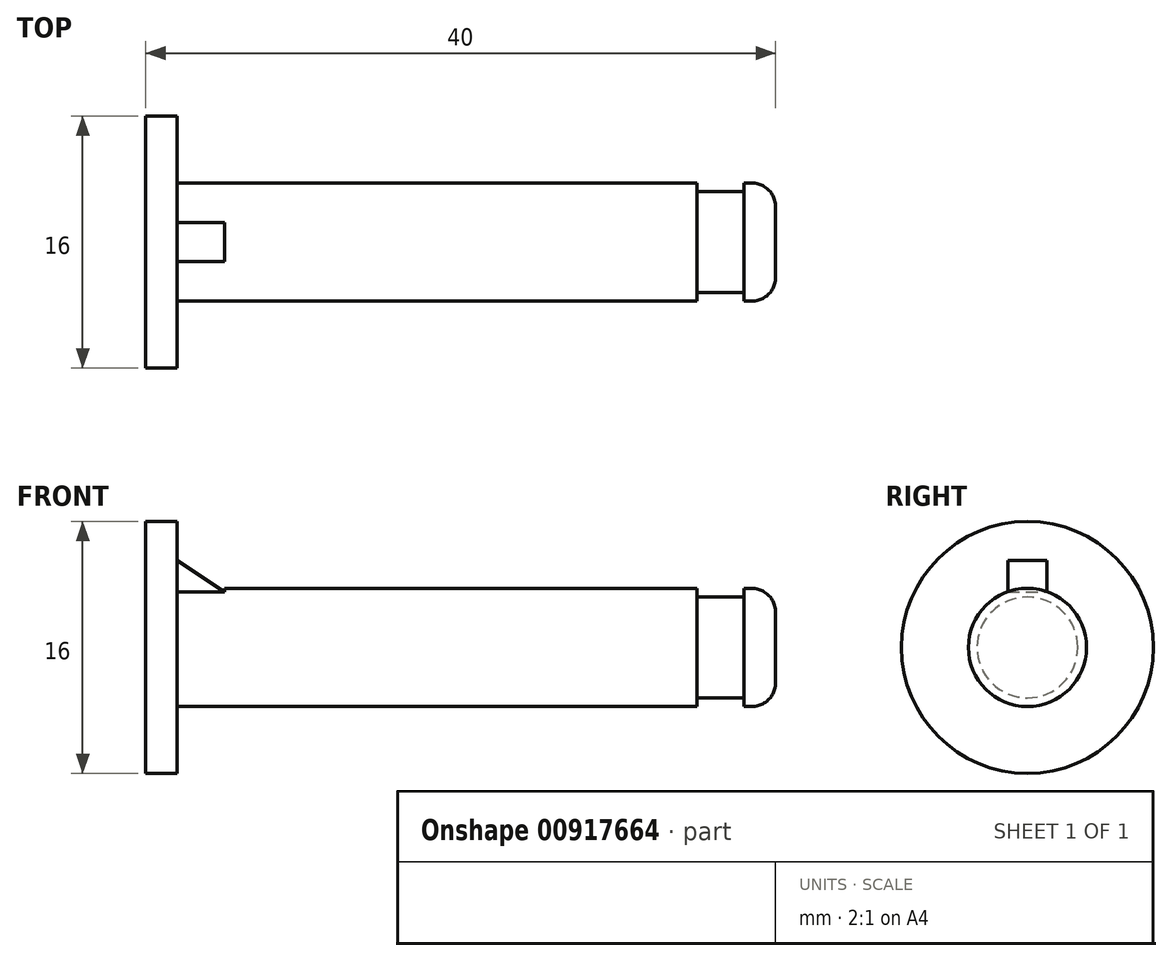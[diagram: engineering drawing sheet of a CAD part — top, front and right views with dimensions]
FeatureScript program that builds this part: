
annotation { "Feature Type Name" : "Feature", "Feature Type Description" : "" }
export const myFeature = defineFeature(function(context is Context, id is Id, definition is map)
    precondition{}
    {
        {
            var Q0;
            Q0=qCreatedBy(makeId("Front.planeOp"),FACE);
            var sketch = newSketch(context, id + "F0", { "sketchPlane" : qUnion([Q0])});
            skLineSegment(sketch, "E0", {"start": v(0, 0) * mm, "end": v(0, 8) * mm});
            skLineSegment(sketch, "E1", {"start": v(0, 8) * mm, "end": v(2, 8) * mm});
            skLineSegment(sketch, "E2", {"start": v(2, 8) * mm, "end": v(2, 3.75) * mm});
            skLineSegment(sketch, "E3", {"start": v(2, 3.75) * mm, "end": v(35, 3.75) * mm});
            skLineSegment(sketch, "E4", {"start": v(35, 3.75) * mm, "end": v(35, 3.2) * mm});
            skLineSegment(sketch, "E5", {"start": v(35, 3.2) * mm, "end": v(38, 3.2) * mm});
            skLineSegment(sketch, "E6", {"start": v(38, 3.2) * mm, "end": v(38, 3.75) * mm});
            skLineSegment(sketch, "E7", {"start": v(38, 3.75) * mm, "end": v(40, 3.75) * mm});
            skLineSegment(sketch, "E8", {"start": v(40, 3.75) * mm, "end": v(40, 0) * mm});
            skLineSegment(sketch, "E9", {"start": v(0, 0) * mm, "end": v(40, 0) * mm});
            skSolve(sketch);
        }
        {
            var Q0;
            Q0 = qSketchRegion(id + "F0", true);
            var Q1;
            Q1=sQuery(id+"F0.wireOp",EDGE,"E9");
            revolve(context, id + "F1", {"surfaceOperationType" : NewSurfaceOperationType.NEW, "entities" : qUnion([Q0]), "axis" : qUnion([Q1]), "revolveType" : RevolveType.FULL});
        }
        {
            var Q0;
            Q0=makeQuery(id+"F1.opRevolve","SWEPT_EDGE",EDGE,{"disambiguationData":[OSD([sQuery(id+"F0.wireOp",EDGE,"E7"),sQuery(id+"F0.wireOp",EDGE,"E8")])]});
            fillet(context, id + "F2", {"entities" : qUnion([Q0]), "radius" : 1.5 * mm, "tangentPropagation" : true, "allowEdgeOverflow" : false});
        }
        {
            var Q0;
            Q0=makeQuery(id+"F1.opRevolve","SWEPT_FACE",FACE,{"disambiguationData":[OSD([sQuery(id+"F0.wireOp",EDGE,"E2")])]});
            var sketch = newSketch(context, id + "F3", { "sketchPlane" : qUnion([Q0])});
            skLineSegment(sketch, "E10", {"start": v(-1.25, 3.54) * mm, "end": v(-1.25, 5.54) * mm});
            skLineSegment(sketch, "E11", {"start": v(-1.25, 5.54) * mm, "end": v(1.25, 5.54) * mm});
            skLineSegment(sketch, "E12", {"start": v(1.25, 5.54) * mm, "end": v(1.25, 3.54) * mm});
            skSolve(sketch);
        }
        {
            var Q0;
            {var subQ0=sQuery(id+"F3.wireOp",EDGE,"E10");Q0=makeQuery(id+"F3.imprint","IMPRINT",FACE,{"disambiguationData":[TD([[makeQuery(id+"F3.imprint","IMPRINT",EDGE,{"derivedFrom":subQ0}),-1.0]])]});}
            extrude(context, id + "F4", {"entities" : qUnion([Q0]), "operationType" : NewBodyOperationType.ADD, "depth" : 3 * mm, "offsetDistance" : 25 * mm});
        }
        {
            var Q0;
            Q0=makeQuery(id+"F4.opExtrude","SWEPT_FACE",FACE,{"disambiguationData":[OSD([sQuery(id+"F3.wireOp",EDGE,"E12")])]});
            var sketch = newSketch(context, id + "F5", { "sketchPlane" : qUnion([Q0])});
            skLineSegment(sketch, "E13", {"start": v(-2, 5.54) * mm, "end": v(-5, 3.54) * mm});
            skSolve(sketch);
        }
        {
            var Q0;
            Q0=makeQuery(id+"F5.imprint","IMPRINT",FACE,{"disambiguationData":[TD([[makeQuery(id+"F5.imprint","IMPRINT",EDGE,{"derivedFrom":sQuery(id+"F5.wireOp",EDGE,"E13")}),-1.0]])]});
            extrude(context, id + "F6", {"entities" : qUnion([Q0]), "operationType" : NewBodyOperationType.REMOVE, "oppositeDirection" : true, "depth" : 25 * mm, "offsetDistance" : 25 * mm});
        }
    });
